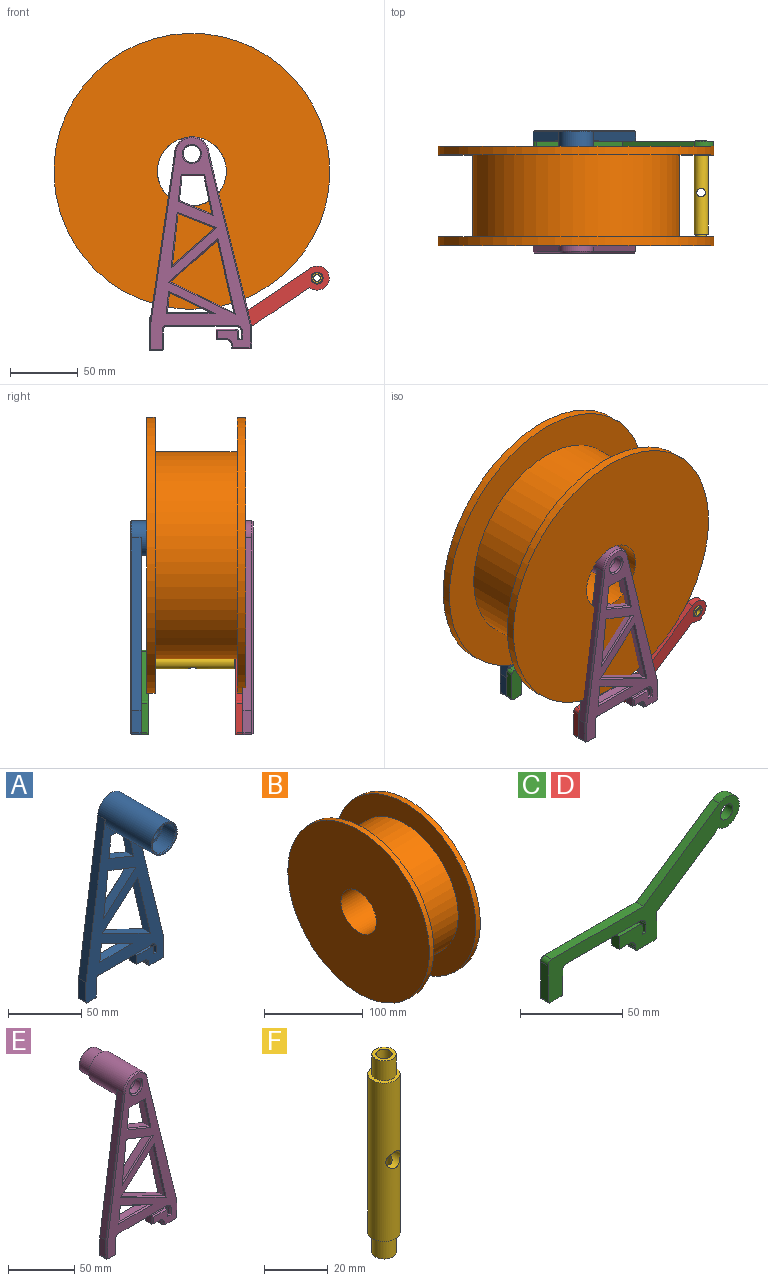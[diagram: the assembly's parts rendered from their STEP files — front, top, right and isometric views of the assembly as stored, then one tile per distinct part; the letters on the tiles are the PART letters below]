
ASSEMBLY  parts=6 mates=11
PART A: 84 faces, bbox 75.4x52.1x158.3 mm
  f0: plane 34.35x30.35mm, normal (0.66,0,-0.75), area 326mm2, adj f1,f36,f37,f71
  f1: plane 52.94x12.1mm, normal (-0.97,0,-0.22), area 386.2mm2, adj f0,f36,f37,f73
  f2: plane 15.24x7.11mm, normal (1,0,0), area 108.4mm2, adj f3,f32,f37,f60
  f3: plane 127x31.44mm, normal (0.97,0,0.24), area 930.5mm2, adj f2,f4,f37,f62
  f4: cylinder r=12.7mm len=51.56mm, axis (0,1,0), area 3830.7mm2, adj f3,f5,f37,f40,f64
  f5: plane 127x18.6mm, normal (-0.99,0,0.14), area 912.9mm2, adj f4,f6,f37,f66
  f6: plane 16.51x7.11mm, normal (-1,0,0), area 117.4mm2, adj f5,f7,f37,f68
  f7: cylinder r=1.27mm len=7.11mm, axis (0,1,0), area 14.2mm2, adj f6,f8,f37,f70
  f8: plane 7.62x7.11mm, normal (0,0,-1), area 54.2mm2, adj f7,f9,f37,f69
  f9: cylinder r=1.27mm len=7.11mm, axis (0,1,0), area 14.2mm2, adj f8,f10,f37,f67
  f10: plane 13.97x7.11mm, normal (1,0,0), area 99.4mm2, adj f9,f11,f37,f65
  f11: cylinder r=2.54mm len=7.11mm, axis (0,1,0), area 28.4mm2, adj f10,f12,f37,f63
  f12: plane 51.31x7.11mm, normal (0,0,-1), area 364.9mm2, adj f11,f13,f37,f61
  f13: cylinder r=3.81mm len=7.11mm, axis (0,1,0), area 42.6mm2, adj f12,f14,f37,f59
  f14: plane 7.11x5.08mm, normal (-1,0,0), area 36.1mm2, adj f13,f15,f37,f57
  f15: plane 7.11x2.16mm, normal (0,0,1), area 15.4mm2, adj f14,f16,f37,f55
  f16: plane 7.11x4.57mm, normal (1,0,0), area 32.5mm2, adj f15,f17,f37,f53
  f17: cylinder r=2.29mm len=7.11mm, axis (0,1,0), area 25.5mm2, adj f16,f18,f37,f51
  f18: plane 14.22x7.11mm, normal (0,0,1), area 101.2mm2, adj f17,f19,f37,f49
  f19: plane 7.62x7.11mm, normal (-1,0,0), area 54.2mm2, adj f18,f20,f37,f47
  f20: plane 7.11x6.86mm, normal (0,0,-1), area 48.8mm2, adj f19,f21,f37,f48
  f21: cylinder r=4.57mm len=7.11mm, axis (0,1,0), area 51.1mm2, adj f20,f22,f37,f50
  f22: plane 7.11x1.02mm, normal (-1,0,0), area 7.2mm2, adj f21,f23,f37,f52
  f23: cylinder r=1.27mm len=7.11mm, axis (0,1,0), area 14.2mm2, adj f22,f24,f37,f54
  f24: plane 12.32x7.11mm, normal (0,0,-1), area 87.6mm2, adj f23,f32,f37,f56
  f25: plane 14.62x7.11mm, normal (0.99,0,-0.11), area 104.6mm2, adj f26,f33,f37,f83
  f26: plane 30.27x14.62mm, normal (-0.43,0,-0.9), area 239.1mm2, adj f25,f33,f37,f81
  f27: plane 27.97x7.11mm, normal (-0.98,0,-0.2), area 203.2mm2, adj f28,f34,f37,f80
  f28: plane 23.8x9.8mm, normal (0.38,0,0.92), area 183mm2, adj f27,f29,f37,f78
  f29: plane 18.17x7.11mm, normal (0.99,0,-0.11), area 130mm2, adj f28,f34,f37,f77
  f30: plane 37.91x7.11mm, normal (0.99,0,-0.11), area 271.2mm2, adj f31,f35,f37,f76
  f31: plane 27.02x10.47mm, normal (-0.36,0,-0.93), area 206.1mm2, adj f30,f35,f37,f74
  f32: cylinder r=1.27mm len=7.11mm, axis (0,1,0), area 14.2mm2, adj f2,f24,f37,f58
  f33: plane 31.84x7.11mm, normal (0,0,1), area 226.5mm2, adj f25,f26,f37,f82
  f34: plane 16.01x7.11mm, normal (0,0,-1), area 113.9mm2, adj f27,f29,f37,f79
  f35: plane 31.11x27.44mm, normal (-0.66,0,0.75), area 295mm2, adj f30,f31,f37,f75
  f36: plane 46.45x22.6mm, normal (0.44,0,0.9), area 367.4mm2, adj f0,f1,f37,f72
  f37: plane 144.78x75.44mm, normal (0,-1,0), area 4330.9mm2, adj f0,f1,f2,f3,f4,f5,f6,f7
  f38: plane 155.72x73.68mm, normal (0,1,0), area 3853.2mm2, adj f46,f47,f48,f49,f50,f51,f52,f53
  f39: cylinder r=11.18mm len=22.35mm, axis (0,1,0), area 838.3mm2, adj f43,f45
  f40: plane 25.4x25.4mm, normal (0,-1,0), area 59mm2, adj f4,f45
  f41: plane 18.8x18.8mm, normal (0,-1,0), area 150.8mm2, adj f42,f44
  f42: cylinder r=9.4mm len=31.75mm, axis (0,1,0), area 1874.8mm2, adj f41,f43
  f43: plane 22.35x22.35mm, normal (0,-1,0), area 114.9mm2, adj f39,f42
  f44: cylinder r=6.35mm len=12.7mm, axis (0,-1,0), area 283.8mm2, adj f41,f46
  f45: torus R=11.94mm, axis (0,-1,0), area 86.1mm2, adj f39,f40
  f46: cone r=7.23mm half-angle=60deg, axis (0,1,0), area 43.3mm2, adj f38,f44
  f47: plane 7.62x0.88mm, normal (-0.5,0.87,0), area 6.8mm2, adj f19,f38,f48,f49
  f48: plane 6.86x0.88mm, normal (0,0.87,-0.5), area 6.5mm2, adj f20,f38,f47,f50
  f49: plane 14.22x0.88mm, normal (0,0.87,0.5), area 14mm2, adj f18,f38,f47,f51
  f50: cone r=5.45mm half-angle=60deg, axis (0,1,0), area 8mm2, adj f21,f38,f48,f52
  f51: cone r=2.29mm half-angle=60deg, axis (0,-1,0), area 2.9mm2, adj f17,f38,f49,f53
  f52: plane 1.02x0.88mm, normal (-0.5,0.87,0), area 1mm2, adj f22,f38,f50,f54
  f53: plane 5.45x0.88mm, normal (0.5,0.87,0), area 5.1mm2, adj f16,f38,f51,f55
  f54: cone r=1.27mm half-angle=60deg, axis (0,-1,0), area 1.3mm2, adj f23,f38,f52,f56
  f55: plane 3.92x0.88mm, normal (0,0.87,0.5), area 3.1mm2, adj f15,f38,f53,f57
  f56: plane 12.32x0.88mm, normal (0,0.87,-0.5), area 12.5mm2, adj f24,f38,f54,f58
  f57: plane 5.96x0.88mm, normal (-0.5,0.87,0), area 5.6mm2, adj f14,f38,f55,f59
  f58: cone r=1.27mm half-angle=60deg, axis (0,-1,0), area 1.3mm2, adj f32,f38,f56,f60
  f59: cone r=4.69mm half-angle=60deg, axis (0,1,0), area 6.8mm2, adj f13,f38,f57,f61
  f60: plane 15.24x0.88mm, normal (0.5,0.87,0), area 15.4mm2, adj f2,f38,f58,f62
  f61: plane 51.31x0.88mm, normal (0,0.87,-0.5), area 52.1mm2, adj f12,f38,f59,f63
  f62: plane 127.11x32.32mm, normal (0.49,0.87,0.12), area 132.9mm2, adj f3,f38,f60,f64
  f63: cone r=3.42mm half-angle=60deg, axis (0,1,0), area 4.8mm2, adj f11,f38,f61,f65
  f64: cone r=12.7mm half-angle=60deg, axis (0,-1,0), area 39.2mm2, adj f4,f38,f62,f66
  f65: plane 13.97x0.88mm, normal (0.5,0.87,0), area 14.2mm2, adj f10,f38,f63,f67
  f66: plane 127.07x19.48mm, normal (-0.49,0.87,0.07), area 130.4mm2, adj f5,f38,f64,f68
  f67: cone r=1.27mm half-angle=60deg, axis (0,-1,0), area 1.3mm2, adj f9,f38,f65,f69
  f68: plane 16.51x0.88mm, normal (-0.5,0.87,0), area 16.7mm2, adj f6,f38,f66,f70
  f69: plane 7.62x0.88mm, normal (0,0.87,-0.5), area 7.7mm2, adj f8,f38,f67,f70
  f70: cone r=1.27mm half-angle=60deg, axis (0,-1,0), area 1.3mm2, adj f7,f38,f68,f69
  f71: plane 36.45x32.2mm, normal (0.33,0.87,-0.37), area 48mm2, adj f0,f38,f72,f73
  f72: plane 49.29x24.19mm, normal (0.22,0.87,0.45), area 54.1mm2, adj f36,f38,f71,f73
  f73: plane 56.18x13.37mm, normal (-0.49,0.87,-0.11), area 56.9mm2, adj f1,f38,f71,f72
  f74: plane 29.44x11.7mm, normal (-0.18,0.87,-0.47), area 30.8mm2, adj f31,f38,f75,f76
  f75: plane 33.89x29.9mm, normal (-0.33,0.87,0.37), area 44mm2, adj f35,f38,f74,f76
  f76: plane 41.31x5.2mm, normal (0.5,0.87,-0.05), area 40.5mm2, adj f30,f38,f74,f75
  f77: plane 19.62x2.9mm, normal (0.5,0.87,-0.05), area 19.3mm2, adj f29,f38,f78,f79
  f78: plane 25.95x11.24mm, normal (0.19,0.87,0.46), area 27.3mm2, adj f28,f38,f77,f80
  f79: plane 17.52x0.88mm, normal (0,0.87,-0.5), area 17mm2, adj f34,f38,f77,f80
  f80: plane 30.3x7.03mm, normal (-0.49,0.87,-0.1), area 30.2mm2, adj f27,f38,f78,f79
  f81: plane 34.86x16.83mm, normal (-0.22,0.87,-0.45), area 36.7mm2, adj f26,f38,f82,f83
  f82: plane 36.67x0.88mm, normal (0,0.87,0.5), area 34.8mm2, adj f33,f38,f81,f83
  f83: plane 16.83x2.56mm, normal (0.5,0.87,-0.05), area 16.1mm2, adj f25,f38,f81,f82
PART B: 8 faces, bbox 73x203.2x203.2 mm
  f0: cylinder r=101.6mm len=203.2mm, axis (-1,0,0), area 4053.7mm2, adj f1,f2
  f1: plane 203.2x203.2mm, normal (1,0,0), area 14187.8mm2, adj f0,f3
  f2: plane 203.2x203.2mm, normal (-1,0,0), area 30402.4mm2, adj f0,f7
  f3: cylinder r=76.2mm len=152.4mm, axis (-1,0,0), area 28882.3mm2, adj f1,f6
  f4: cylinder r=101.6mm len=203.2mm, axis (-1,0,0), area 4053.7mm2, adj f5,f6
  f5: plane 203.2x203.2mm, normal (1,0,0), area 30402.4mm2, adj f4,f7
  f6: plane 203.2x203.2mm, normal (-1,0,0), area 14187.8mm2, adj f3,f4
  f7: cylinder r=25.4mm len=73.03mm, axis (1,0,0), area 11654.3mm2, adj f2,f5
PART C: 29 faces, bbox 132.5x5.1x62.3 mm
  f0: cylinder r=1.27mm len=5.08mm, axis (0,1,0), area 10.1mm2, adj f1,f26,f27,f28
  f1: plane 15.24x5.08mm, normal (1,0,0), area 77.4mm2, adj f0,f2,f27,f28
  f2: plane 42.6x28.67mm, normal (0.56,0,-0.83), area 260.8mm2, adj f1,f3,f27,f28
  f3: cylinder r=8.89mm len=17.78mm, axis (0,1,0), area 198.6mm2, adj f2,f4,f27,f28
  f4: plane 52.68x35.45mm, normal (-0.56,0,0.83), area 322.6mm2, adj f3,f5,f27,f28
  f5: plane 63.47x5.08mm, normal (0,0,1), area 322.4mm2, adj f4,f6,f27,f28
  f6: cylinder r=2.54mm len=5.08mm, axis (0,1,0), area 20.3mm2, adj f5,f7,f27,f28
  f7: plane 21.56x5.08mm, normal (-1,0,0), area 109.5mm2, adj f6,f8,f27,f28
  f8: cylinder r=1.27mm len=5.08mm, axis (0,1,0), area 10.1mm2, adj f7,f9,f27,f28
  f9: plane 7.62x5.08mm, normal (0,0,-1), area 38.7mm2, adj f8,f10,f27,f28
  f10: cylinder r=1.27mm len=5.08mm, axis (0,1,0), area 10.1mm2, adj f9,f11,f27,f28
  f11: plane 13.97x5.08mm, normal (1,0,0), area 71mm2, adj f10,f12,f27,f28
  f12: cylinder r=2.54mm len=5.08mm, axis (0,1,0), area 20.3mm2, adj f11,f13,f27,f28
  f13: plane 51.31x5.08mm, normal (0,0,-1), area 260.6mm2, adj f12,f14,f27,f28
  f14: cylinder r=3.81mm len=5.08mm, axis (0,1,0), area 30.4mm2, adj f13,f15,f27,f28
  f15: plane 5.08x5.08mm, normal (-1,0,0), area 25.8mm2, adj f14,f16,f27,f28
  f16: plane 5.08x2.16mm, normal (0,0,1), area 11mm2, adj f15,f17,f27,f28
  f17: plane 5.08x4.57mm, normal (1,0,0), area 23.2mm2, adj f16,f18,f27,f28
  f18: cylinder r=2.29mm len=5.08mm, axis (0,1,0), area 18.2mm2, adj f17,f19,f27,f28
  f19: plane 14.22x5.08mm, normal (0,0,1), area 72.3mm2, adj f18,f20,f27,f28
  f20: plane 7.62x5.08mm, normal (-1,0,0), area 38.7mm2, adj f19,f21,f27,f28
  f21: plane 6.86x5.08mm, normal (0,0,-1), area 34.8mm2, adj f20,f22,f27,f28
  f22: cylinder r=4.57mm len=5.08mm, axis (0,1,0), area 36.5mm2, adj f21,f23,f27,f28
  f23: plane 5.08x1.02mm, normal (-1,0,0), area 5.2mm2, adj f22,f24,f27,f28
  f24: cylinder r=1.27mm len=5.08mm, axis (0,1,0), area 10.1mm2, adj f23,f26,f27,f28
  f25: cylinder r=4.45mm len=8.89mm, axis (0,1,0), area 141.9mm2, adj f27,f28
  f26: plane 12.32x5.08mm, normal (0,0,-1), area 62.6mm2, adj f0,f24,f27,f28
  f27: plane 132.47x62.29mm, normal (0,-1,0), area 1838.6mm2, adj f0,f1,f2,f3,f4,f5,f6,f7
  f28: plane 132.47x62.29mm, normal (0,1,0), area 1838.6mm2, adj f0,f1,f2,f3,f4,f5,f6,f7
PART D: same geometry as C
PART E: 84 faces, bbox 75.4x50.8x157.5 mm
  f0: plane 34.35x30.35mm, normal (0.66,0,-0.75), area 288.8mm2, adj f1,f36,f38,f70
  f1: plane 52.94x12.1mm, normal (-0.97,0,-0.22), area 342.2mm2, adj f0,f36,f38,f72
  f2: plane 15.24x6.3mm, normal (1,0,0), area 96mm2, adj f3,f32,f38,f59
  f3: plane 127x31.44mm, normal (0.97,0,0.24), area 824.3mm2, adj f2,f4,f38,f61
  f4: cylinder r=12.7mm len=36.78mm, axis (0,1,0), area 2683.6mm2, adj f3,f5,f38,f39,f63
  f5: plane 127x18.6mm, normal (-0.99,0,0.14), area 808.7mm2, adj f4,f6,f38,f65
  f6: plane 16.51x6.3mm, normal (-1,0,0), area 104mm2, adj f5,f7,f38,f67
  f7: cylinder r=1.27mm len=6.3mm, axis (0,1,0), area 12.6mm2, adj f6,f8,f38,f69
  f8: plane 7.62x6.3mm, normal (0,0,-1), area 48mm2, adj f7,f9,f38,f68
  f9: cylinder r=1.27mm len=6.3mm, axis (0,1,0), area 12.6mm2, adj f8,f10,f38,f66
  f10: plane 13.97x6.3mm, normal (1,0,0), area 88mm2, adj f9,f11,f38,f64
  f11: cylinder r=2.54mm len=6.3mm, axis (0,1,0), area 25.1mm2, adj f10,f12,f38,f62
  f12: plane 51.31x6.3mm, normal (0,0,-1), area 323.2mm2, adj f11,f13,f38,f60
  f13: cylinder r=3.81mm len=6.3mm, axis (0,1,0), area 37.7mm2, adj f12,f14,f38,f58
  f14: plane 6.3x5.08mm, normal (-1,0,0), area 32mm2, adj f13,f15,f38,f56
  f15: plane 6.3x2.16mm, normal (0,0,1), area 13.6mm2, adj f14,f16,f38,f54
  f16: plane 6.3x4.57mm, normal (1,0,0), area 28.8mm2, adj f15,f17,f38,f52
  f17: cylinder r=2.29mm len=6.3mm, axis (0,1,0), area 22.6mm2, adj f16,f18,f38,f50
  f18: plane 14.22x6.3mm, normal (0,0,1), area 89.6mm2, adj f17,f19,f38,f48
  f19: plane 7.62x6.3mm, normal (-1,0,0), area 48mm2, adj f18,f20,f38,f46
  f20: plane 6.86x6.3mm, normal (0,0,-1), area 43.2mm2, adj f19,f21,f38,f47
  f21: cylinder r=4.57mm len=6.3mm, axis (0,1,0), area 45.2mm2, adj f20,f22,f38,f49
  f22: plane 6.3x1.02mm, normal (-1,0,0), area 6.4mm2, adj f21,f23,f38,f51
  f23: cylinder r=1.27mm len=6.3mm, axis (0,1,0), area 12.6mm2, adj f22,f24,f38,f53
  f24: plane 12.32x6.3mm, normal (0,0,-1), area 77.6mm2, adj f23,f32,f38,f55
  f25: plane 14.62x6.3mm, normal (0.99,0,-0.11), area 92.6mm2, adj f26,f33,f38,f82
  f26: plane 30.27x14.62mm, normal (-0.43,0,-0.9), area 211.8mm2, adj f25,f33,f38,f80
  f27: plane 27.97x6.3mm, normal (-0.98,0,-0.2), area 180mm2, adj f28,f34,f38,f79
  f28: plane 23.8x9.8mm, normal (0.38,0,0.92), area 162.2mm2, adj f27,f29,f38,f77
  f29: plane 18.17x6.3mm, normal (0.99,0,-0.11), area 115.2mm2, adj f28,f34,f38,f76
  f30: plane 37.91x6.3mm, normal (0.99,0,-0.11), area 240.2mm2, adj f31,f35,f38,f75
  f31: plane 27.02x10.47mm, normal (-0.36,0,-0.93), area 182.6mm2, adj f30,f35,f38,f73
  f32: cylinder r=1.27mm len=6.3mm, axis (0,1,0), area 12.6mm2, adj f2,f24,f38,f57
  f33: plane 31.84x6.3mm, normal (0,0,1), area 200.6mm2, adj f25,f26,f38,f81
  f34: plane 16.01x6.3mm, normal (0,0,-1), area 100.9mm2, adj f27,f29,f38,f78
  f35: plane 31.11x27.44mm, normal (-0.66,0,0.75), area 261.3mm2, adj f30,f31,f38,f74
  f36: plane 46.45x22.6mm, normal (0.44,0,0.9), area 325.4mm2, adj f0,f1,f38,f71
  f37: plane 155.96x73.91mm, normal (0,-1,0), area 3970.1mm2, adj f45,f46,f47,f48,f49,f50,f51,f52
  f38: plane 144.78x75.44mm, normal (0,1,0), area 4330.9mm2, adj f0,f1,f2,f3,f4,f5,f6,f7
  f39: plane 25.4x25.4mm, normal (0,1,0), area 149.2mm2, adj f4,f40
  f40: cylinder r=10.67mm len=21.34mm, axis (0,-1,0), area 800.2mm2, adj f39,f83
  f41: plane 19.81x19.81mm, normal (0,1,0), area 30.8mm2, adj f43,f83
  f42: plane 18.8x18.8mm, normal (0,1,0), area 150.8mm2, adj f43,f44
  f43: cylinder r=9.4mm len=43.18mm, axis (0,-1,0), area 2549.8mm2, adj f41,f42
  f44: cylinder r=6.35mm len=12.7mm, axis (0,-1,0), area 251.4mm2, adj f42,f45
  f45: cone r=6.35mm half-angle=30deg, axis (0,-1,0), area 64.5mm2, adj f37,f44
  f46: plane 7.62x1.32mm, normal (-0.87,-0.5,0), area 10.5mm2, adj f19,f37,f47,f48
  f47: plane 6.86x1.32mm, normal (0,-0.5,-0.87), area 9.9mm2, adj f20,f37,f46,f49
  f48: plane 14.22x1.32mm, normal (0,-0.5,0.87), area 21.1mm2, adj f18,f37,f46,f50
  f49: cone r=4.57mm half-angle=30deg, axis (0,-1,0), area 11.9mm2, adj f21,f37,f47,f51
  f50: cone r=1.52mm half-angle=30deg, axis (0,1,0), area 4.6mm2, adj f17,f37,f48,f52
  f51: plane 1.32x1.02mm, normal (-0.87,-0.5,0), area 1.5mm2, adj f22,f37,f49,f53
  f52: plane 5.33x1.32mm, normal (0.87,-0.5,0), area 7.5mm2, adj f16,f37,f50,f54
  f53: cone r=0.51mm half-angle=30deg, axis (0,1,0), area 2.1mm2, adj f23,f37,f51,f55
  f54: plane 3.68x1.32mm, normal (0,-0.5,0.87), area 4.5mm2, adj f15,f37,f52,f56
  f55: plane 12.32x1.32mm, normal (0,-0.5,-0.87), area 18.8mm2, adj f24,f37,f53,f57
  f56: plane 5.84x1.32mm, normal (-0.87,-0.5,0), area 8.3mm2, adj f14,f37,f54,f58
  f57: cone r=0.51mm half-angle=30deg, axis (0,1,0), area 2.1mm2, adj f32,f37,f55,f59
  f58: cone r=3.81mm half-angle=30deg, axis (0,-1,0), area 10mm2, adj f13,f37,f56,f60
  f59: plane 15.24x1.32mm, normal (0.87,-0.5,0), area 23.2mm2, adj f2,f37,f57,f61
  f60: plane 51.31x1.32mm, normal (0,-0.5,-0.87), area 78.2mm2, adj f12,f37,f58,f62
  f61: plane 127.1x32.2mm, normal (0.84,-0.5,0.21), area 199.4mm2, adj f3,f37,f59,f63
  f62: cone r=2.54mm half-angle=30deg, axis (0,-1,0), area 7mm2, adj f11,f37,f60,f64
  f63: cone r=11.94mm half-angle=30deg, axis (0,1,0), area 59.1mm2, adj f4,f37,f61,f65
  f64: plane 13.97x1.32mm, normal (0.87,-0.5,0), area 21.3mm2, adj f10,f37,f62,f66
  f65: plane 127.06x19.37mm, normal (-0.86,-0.5,0.13), area 195.6mm2, adj f5,f37,f63,f67
  f66: cone r=0.51mm half-angle=30deg, axis (0,1,0), area 2.1mm2, adj f9,f37,f64,f68
  f67: plane 16.51x1.32mm, normal (-0.87,-0.5,0), area 25.1mm2, adj f6,f37,f65,f69
  f68: plane 7.62x1.32mm, normal (0,-0.5,-0.87), area 11.6mm2, adj f8,f37,f66,f69
  f69: cone r=0.51mm half-angle=30deg, axis (0,1,0), area 2.1mm2, adj f7,f37,f67,f68
  f70: plane 36.17x31.95mm, normal (0.57,-0.5,-0.65), area 71.7mm2, adj f0,f37,f71,f72
  f71: plane 48.91x23.98mm, normal (0.38,-0.5,0.78), area 80.8mm2, adj f36,f37,f70,f72
  f72: plane 55.75x13.2mm, normal (-0.84,-0.5,-0.19), area 85mm2, adj f1,f37,f70,f71
  f73: plane 29.12x11.54mm, normal (-0.31,-0.5,-0.81), area 45.9mm2, adj f31,f37,f74,f75
  f74: plane 33.52x29.57mm, normal (-0.57,-0.5,0.65), area 65.7mm2, adj f35,f37,f73,f75
  f75: plane 40.85x5.06mm, normal (0.86,-0.5,-0.09), area 60.4mm2, adj f30,f37,f73,f74
  f76: plane 19.42x2.78mm, normal (0.86,-0.5,-0.09), area 28.8mm2, adj f29,f37,f77,f78
  f77: plane 25.66x11.05mm, normal (0.33,-0.5,0.8), area 40.8mm2, adj f28,f37,f76,f79
  f78: plane 17.31x1.32mm, normal (0,-0.5,-0.87), area 25.4mm2, adj f34,f37,f76,f79
  f79: plane 29.99x6.87mm, normal (-0.85,-0.5,-0.18), area 45.1mm2, adj f27,f37,f77,f78
  f80: plane 34.24x16.54mm, normal (-0.38,-0.5,-0.78), area 54.6mm2, adj f26,f37,f81,f82
  f81: plane 36.02x1.32mm, normal (0,-0.5,0.87), area 51.7mm2, adj f33,f37,f80,f82
  f82: plane 16.54x2.42mm, normal (0.86,-0.5,-0.09), area 23.9mm2, adj f25,f37,f80,f81
  f83: torus R=9.91mm, axis (0,1,0), area 78.1mm2, adj f40,f41
PART F: 10 faces, bbox 10.2x10.2x76.2 mm
  f0: cylinder r=3.81mm len=7.62mm, axis (0,0,-1), area 182.4mm2, adj f1,f4
  f1: plane 7.62x7.62mm, normal (0,0,-1), area 25.3mm2, adj f0,f9
  f2: cylinder r=5.08mm len=60.96mm, axis (0,0,-1), area 1878.8mm2, adj f3,f4,f7
  f3: plane 10.16x10.16mm, normal (0,0,1), area 35.5mm2, adj f2,f5
  f4: plane 10.16x10.16mm, normal (0,0,-1), area 35.5mm2, adj f0,f2
  f5: cylinder r=3.81mm len=7.62mm, axis (0,0,-1), area 182.4mm2, adj f3,f6
  f6: plane 7.62x7.62mm, normal (0,0,1), area 25.3mm2, adj f5,f8
  f7: cylinder r=3.17mm len=10.16mm, axis (0,-1,0), area 136.1mm2, adj f2,f8,f9
  f8: cylinder r=2.54mm len=36.2mm, axis (0,0,-1), area 566.9mm2, adj f6,f7
  f9: cylinder r=2.54mm len=36.2mm, axis (0,0,-1), area 566.9mm2, adj f1,f7
PLACE A t=(-22.13,245.14,-31.06)mm
PLACE B rot(axis=(0,0,-1),90deg) t=(-22.07,233.54,83.16)mm
PLACE C t=(-22.13,237.52,-31.06)mm
PLACE D t=(-22.13,167.67,-31.06)mm
PLACE E t=(-22.13,162.59,-31.06)mm
PLACE F rot(axis=(1,0,0),90deg) t=(70.15,237.7,4.56)mm
MATE cylindrical F.f0 <-> C.f3  axis (0,1,0) through (70.15,165.31,4.56)mm
MATE planar E.f12 <-> A.f12  axis (0,0,-1) through (-15.08,159.44,-31.06)mm
MATE planar D.f1 <-> E.f2  axis (1,0,0) through (22.01,165.13,-38.68)mm
MATE parallel B.f0 <-> E.f38  axis (0,-1,0) through (-22.07,160.52,83.16)mm
MATE planar D.f27 <-> E.f38  axis (0,-1,0) through (12.51,162.59,-22.08)mm
MATE planar A.f4 <-> E.f44  axis (0,-1,0) through (-22.13,193.07,95.94)mm
MATE planar C.f28 <-> A.f37  axis (0,1,0) through (38.92,237.52,-5.74)mm
MATE planar C.f26 <-> A.f24  axis (0,0,-1) through (20.74,234.98,-47.57)mm
MATE cylindrical A.f4 <-> E.f40  axis (0,1,0) through (-22.13,193.84,95.94)mm
MATE planar A.f2 <-> C.f1  axis (1,0,0) through (22.01,241.08,-38.68)mm
MATE planar E.f24 <-> D.f26  axis (0,0,-1) through (14.58,159.44,-47.57)mm
